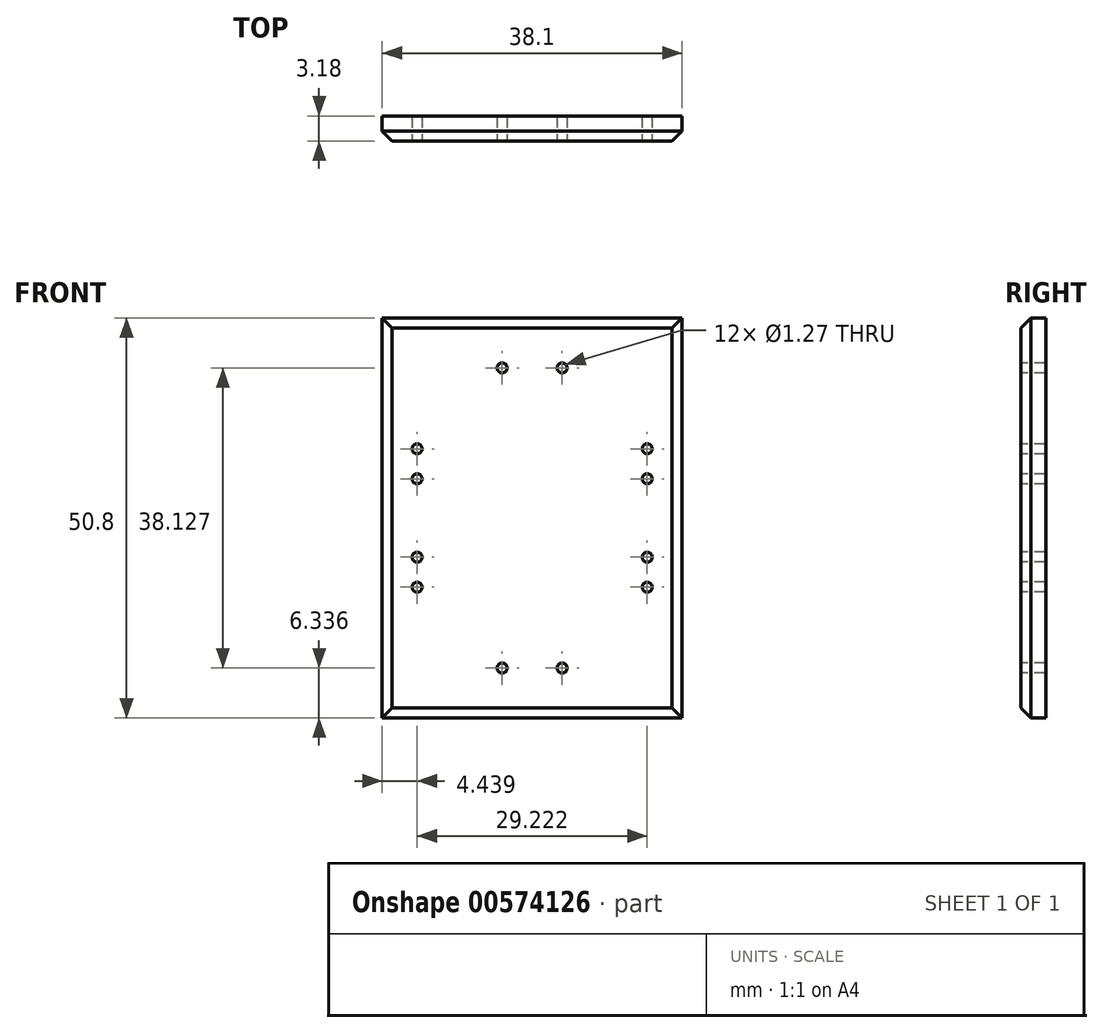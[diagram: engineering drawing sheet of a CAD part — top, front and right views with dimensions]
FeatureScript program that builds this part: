
annotation { "Feature Type Name" : "Feature", "Feature Type Description" : "" }
export const myFeature = defineFeature(function(context is Context, id is Id, definition is map)
    precondition{}
    {
        {
            var Q0;
            Q0=qCreatedBy(makeId("Front.planeOp"),FACE);
            var sketch = newSketch(context, id + "F0", { "sketchPlane" : qUnion([Q0])});
            skLineSegment(sketch, "E0.bottom", {"start": v(19.05, 25.4) * mm, "end": v(-19.05, 25.4) * mm});
            skLineSegment(sketch, "E0.top", {"start": v(19.05, -25.4) * mm, "end": v(-19.05, -25.4) * mm});
            skLineSegment(sketch, "E0.left", {"start": v(19.05, 25.4) * mm, "end": v(19.05, -25.4) * mm});
            skLineSegment(sketch, "E0.right", {"start": v(-19.05, 25.4) * mm, "end": v(-19.05, -25.4) * mm});
            skPoint(sketch, "E0.middle", {"position": v(0, 0) * mm});
            skSolve(sketch);
        }
        {
            var Q0;
            Q0=makeQuery(id+"F0.imprint","IMPRINT",FACE,{"disambiguationData":[TD([[makeQuery(id+"F0.imprint","IMPRINT",EDGE,{"derivedFrom":sQuery(id+"F0.wireOp",EDGE,"E0.bottom")}),1.0]])]});
            extrude(context, id + "F1", {"entities" : qUnion([Q0]), "depth" : 3.17 * mm});
        }
        {
            var Q0;
            Q0=makeQuery(id+"F1.opExtrude","CAP_FACE",FACE,{"disambiguationData":[OSD([sQuery(id+"F0.wireOp",EDGE,"E0.bottom"),sQuery(id+"F0.wireOp",EDGE,"E0.top"),sQuery(id+"F0.wireOp",EDGE,"E0.left"),sQuery(id+"F0.wireOp",EDGE,"E0.right")])],"isStart":false});
            chamfer(context, id + "F2", {"entities" : qUnion([Q0]), "width" : 1.27 * mm, "tangentPropagation" : true});
        }
        {
            var Q0;
            Q0=makeQuery(id+"F1.opExtrude","CAP_FACE",FACE,{"disambiguationData":[OSD([sQuery(id+"F0.wireOp",EDGE,"E0.bottom"),sQuery(id+"F0.wireOp",EDGE,"E0.top"),sQuery(id+"F0.wireOp",EDGE,"E0.left"),sQuery(id+"F0.wireOp",EDGE,"E0.right")])],"isStart":false});
            var sketch = newSketch(context, id + "F3", { "sketchPlane" : qUnion([Q0])});
            skLineSegment(sketch, "E1.0", {"start": v(19.05, 25.4) * mm, "end": v(-19.05, 25.4) * mm});
            skLineSegment(sketch, "E2", {"start": v(0, 25.4) * mm, "end": v(0, -13.77) * mm, "construction": true});
            skLineSegment(sketch, "E3.0", {"start": v(-19.05, 25.4) * mm, "end": v(-19.05, -25.4) * mm});
            skLineSegment(sketch, "E4", {"start": v(-19.05, 0) * mm, "end": v(23.52, 0) * mm, "construction": true});
            skPoint(sketch, "E5", {"position": v(-3.81, 19.06) * mm});
            skPoint(sketch, "E6", {"position": v(-14.61, 8.79) * mm});
            skPoint(sketch, "E7", {"position": v(-14.61, 4.98) * mm});
            skPoint(sketch, "E8.MirrorP", {"position": v(3.8, 19.06) * mm});
            skPoint(sketch, "E9.MirrorP", {"position": v(14.61, 4.98) * mm});
            skPoint(sketch, "E10.MirrorP", {"position": v(14.61, 8.79) * mm});
            skPoint(sketch, "E11.MirrorP", {"position": v(-14.61, -4.98) * mm});
            skPoint(sketch, "E12.MirrorP", {"position": v(-3.8, -19.06) * mm});
            skPoint(sketch, "E13.MirrorP", {"position": v(14.61, -8.79) * mm});
            skPoint(sketch, "E14.MirrorP", {"position": v(-14.61, -8.79) * mm});
            skPoint(sketch, "E15.MirrorP", {"position": v(14.61, -4.98) * mm});
            skPoint(sketch, "E16.MirrorP", {"position": v(3.8, -19.06) * mm});
            skSolve(sketch);
        }
        {
            var Q0;
            Q0=sQuery(id+"F3.wireOp",VERTEX,"E6");
            var Q1;
            Q1=sQuery(id+"F3.wireOp",VERTEX,"E16.MirrorP");
            var Q2;
            Q2=sQuery(id+"F3.wireOp",VERTEX,"E15.MirrorP");
            var Q3;
            Q3=sQuery(id+"F3.wireOp",VERTEX,"E7");
            var Q4;
            Q4=sQuery(id+"F3.wireOp",VERTEX,"E8.MirrorP");
            var Q5;
            Q5=sQuery(id+"F3.wireOp",VERTEX,"E13.MirrorP");
            var Q6;
            Q6=sQuery(id+"F3.wireOp",VERTEX,"E5");
            var Q7;
            Q7=sQuery(id+"F3.wireOp",VERTEX,"E14.MirrorP");
            var Q8;
            Q8=sQuery(id+"F3.wireOp",VERTEX,"E9.MirrorP");
            var Q9;
            Q9=sQuery(id+"F3.wireOp",VERTEX,"E10.MirrorP");
            var Q10;
            Q10=sQuery(id+"F3.wireOp",VERTEX,"E11.MirrorP");
            var Q11;
            Q11=sQuery(id+"F3.wireOp",VERTEX,"E12.MirrorP");
            var Q12;
            Q12=makeQuery(id+"F1.opExtrude","SWEPT_BODY",BODY,{"disambiguationData":[OSD([sQuery(id+"F0.wireOp",EDGE,"E0.bottom"),sQuery(id+"F0.wireOp",EDGE,"E0.top"),sQuery(id+"F0.wireOp",EDGE,"E0.left"),sQuery(id+"F0.wireOp",EDGE,"E0.right")])]});
            hole(context, id + "F4", {"style" : HoleStyle.SIMPLE, "endStyle" : HoleEndStyle.THROUGH, "holeDiameter" : 1.27 * mm, "locations" : qUnion([Q0, Q1, Q2, Q3, Q4, Q5, Q6, Q7, Q8, Q9, Q10, Q11]), "scope" : qUnion([Q12]), "isTappedThrough" : true});
        }
    });
